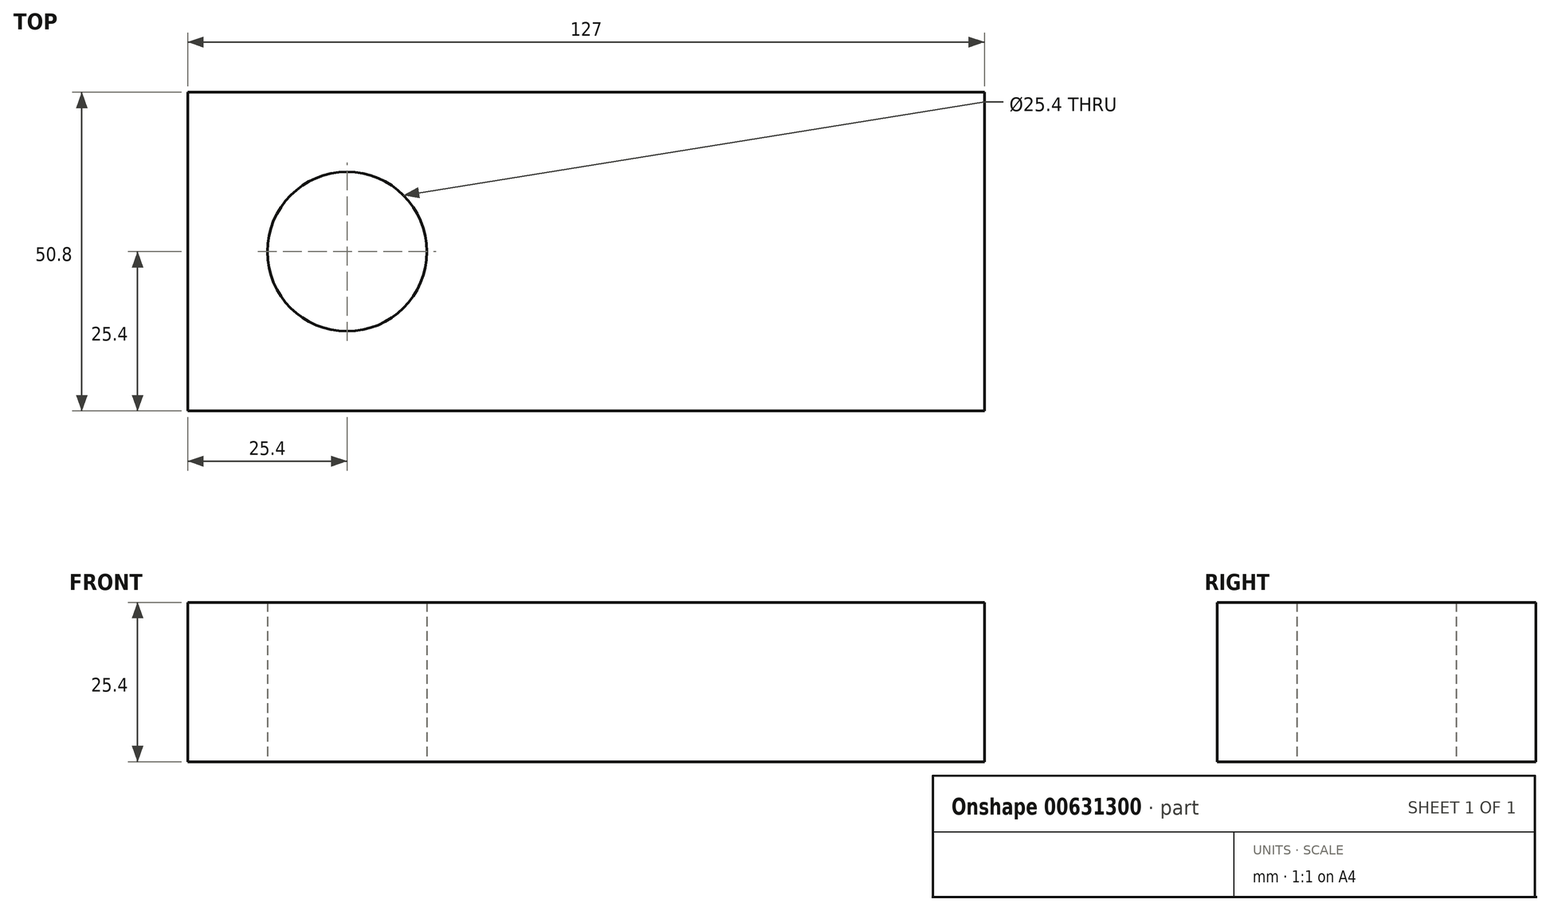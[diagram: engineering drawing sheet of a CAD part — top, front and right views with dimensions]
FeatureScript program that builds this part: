
annotation { "Feature Type Name" : "Feature", "Feature Type Description" : "" }
export const myFeature = defineFeature(function(context is Context, id is Id, definition is map)
    precondition{}
    {
        {
            var Q0;
            Q0=qCreatedBy(makeId("Top.planeOp"),FACE);
            var sketch = newSketch(context, id + "F0", { "sketchPlane" : qUnion([Q0])});
            skLineSegment(sketch, "E0.bottom", {"start": v(-25.4, -25.4) * mm, "end": v(101.6, -25.4) * mm});
            skLineSegment(sketch, "E0.top", {"start": v(-25.4, 25.4) * mm, "end": v(101.6, 25.4) * mm});
            skLineSegment(sketch, "E0.left", {"start": v(-25.4, -25.4) * mm, "end": v(-25.4, 25.4) * mm});
            skLineSegment(sketch, "E0.right", {"start": v(101.6, -25.4) * mm, "end": v(101.6, 25.4) * mm});
            skCircle(sketch, "E1", {"center": v(0, 0) * mm, "radius": 12.7 * mm});
            skSolve(sketch);
        }
        {
            var Q0;
            Q0=makeQuery(id+"F0.imprint","IMPRINT",FACE,{"disambiguationData":[TD([[makeQuery(id+"F0.imprint","IMPRINT",EDGE,{"derivedFrom":sQuery(id+"F0.wireOp",EDGE,"E0.bottom")}),1.0]])]});
            extrude(context, id + "F1", {"entities" : qUnion([Q0]), "depth" : 25.4 * mm, "offsetDistance" : 25.4 * mm});
        }
    });
